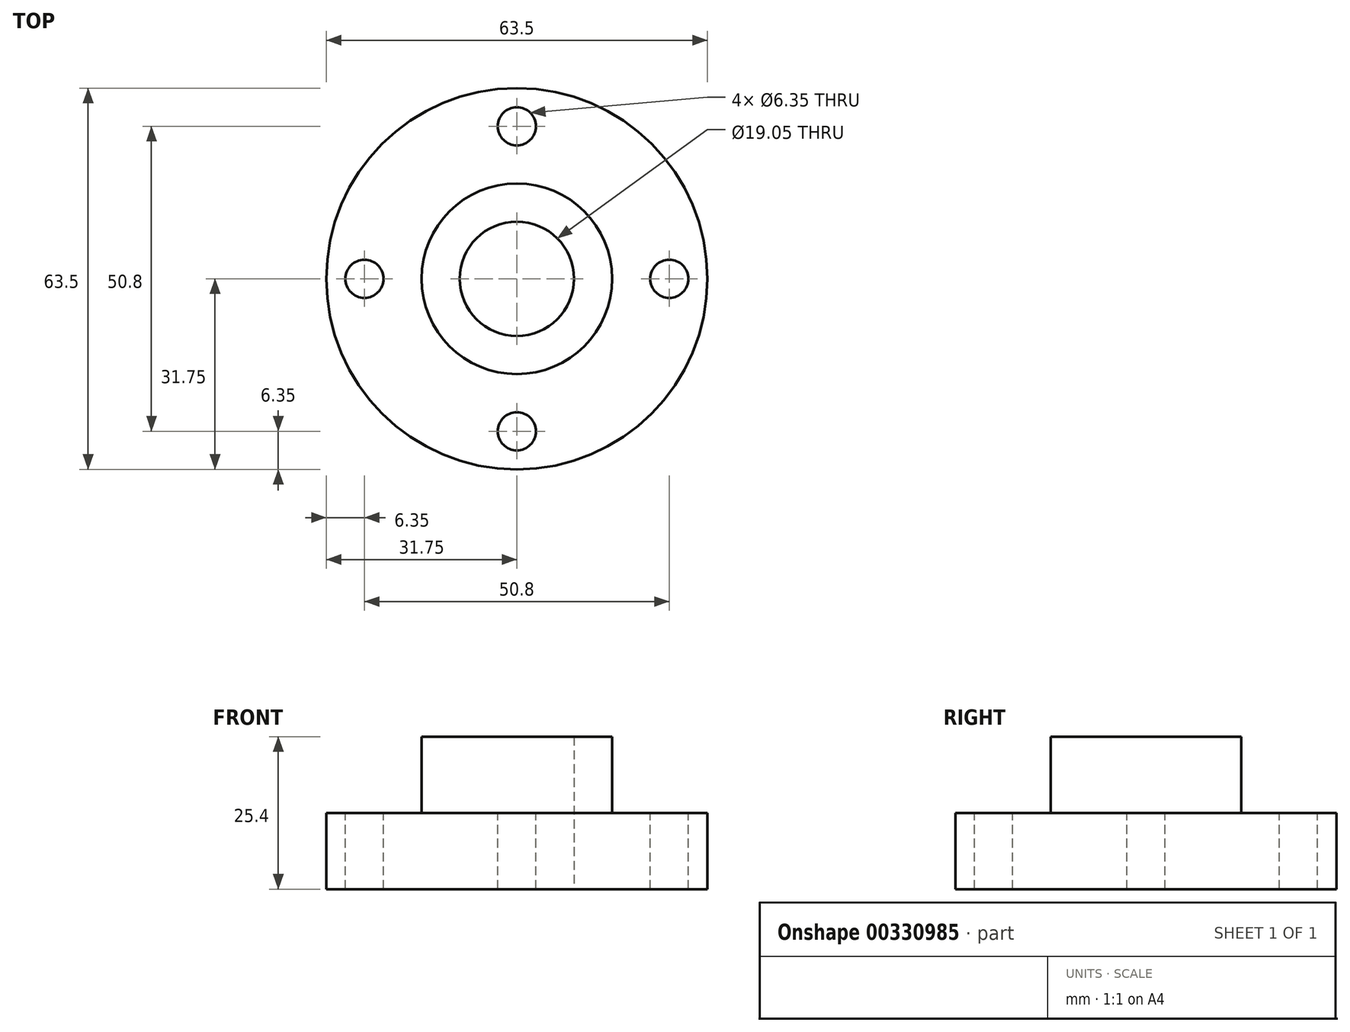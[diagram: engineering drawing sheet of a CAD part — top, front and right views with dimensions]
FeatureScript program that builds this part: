
annotation { "Feature Type Name" : "Feature", "Feature Type Description" : "" }
export const myFeature = defineFeature(function(context is Context, id is Id, definition is map)
    precondition{}
    {
        {
            var Q0;
            Q0=qCreatedBy(makeId("Top.planeOp"),FACE);
            var sketch = newSketch(context, id + "F0", { "sketchPlane" : qUnion([Q0])});
            skCircle(sketch, "E0", {"center": v(0, 0) * mm, "radius": 31.75 * mm});
            skCircle(sketch, "E1", {"center": v(0, 0) * mm, "radius": 25.4 * mm});
            skCircle(sketch, "E2", {"center": v(0, 25.4) * mm, "radius": 3.18 * mm});
            skCircle(sketch, "E3.1.0", {"center": v(-25.4, 0) * mm, "radius": 3.18 * mm});
            skCircle(sketch, "E3.2.0", {"center": v(0, -25.4) * mm, "radius": 3.18 * mm});
            skCircle(sketch, "E3.3.0", {"center": v(25.4, 0) * mm, "radius": 3.18 * mm});
            skSolve(sketch);
        }
        {
            var Q0;
            Q0=makeQuery(id+"F0.imprint","IMPRINT",FACE,{"disambiguationData":[TD([[makeQuery(id+"F0.imprint","IMPRINT",EDGE,{"derivedFrom":sQuery(id+"F0.wireOp",EDGE,"E0")}),1.0]])]});
            var Q1;
            {var subQ1=sQuery(id+"F0.wireOp",EDGE,"E1");var subQ8=sQuery(id+"F0.wireOp",EDGE,"E2");var subQ11=makeQuery(id+"F0.imprint","INTERSECT",VERTEX,{"disambiguationData":[OD(0.0)],"derivedFrom":[subQ1,subQ8]});Q1=makeQuery(id+"F0.imprint","IMPRINT",FACE,{"disambiguationData":[TD([[makeQuery(id+"F0.imprint","IMPRINT",EDGE,{"disambiguationData":[TD([[subQ11,1.0]])],"derivedFrom":subQ1}),1.0]])]});}
            extrude(context, id + "F1", {"entities" : qUnion([Q0, Q1]), "oppositeDirection" : true, "depth" : 12.7 * mm});
        }
        {
            var Q0;
            Q0=qCreatedBy(makeId("Top.planeOp"),FACE);
            var sketch = newSketch(context, id + "F2", { "sketchPlane" : qUnion([Q0])});
            skCircle(sketch, "E4", {"center": v(0, 0) * mm, "radius": 15.88 * mm});
            skCircle(sketch, "E5", {"center": v(0, 0) * mm, "radius": 9.53 * mm});
            skSolve(sketch);
        }
        {
            var Q0;
            Q0 = qSketchRegion(id + "F2", true);
            extrude(context, id + "F3", {"entities" : qUnion([Q0]), "operationType" : NewBodyOperationType.ADD, "depth" : 12.7 * mm});
        }
        {
            var Q0;
            Q0=makeQuery(id+"F3.boolean.opBoolean","SPLIT",FACE,{"disambiguationData":[TD([makeQuery(id+"F3.opExtrude","SWEPT_FACE",FACE,{"disambiguationData":[OSD([sQuery(id+"F2.wireOp",EDGE,"E5")])]})])],"derivedFrom":makeQuery(id+"F1.opExtrude","CAP_FACE",FACE,{"disambiguationData":[OSD([sQuery(id+"F0.wireOp",EDGE,"E0"),sQuery(id+"F0.wireOp",EDGE,"E2"),sQuery(id+"F0.wireOp",EDGE,"E3.1.0"),sQuery(id+"F0.wireOp",EDGE,"E3.2.0"),sQuery(id+"F0.wireOp",EDGE,"E3.3.0")])],"isStart":true})});
            extrude(context, id + "F4", {"entities" : qUnion([Q0]), "operationType" : NewBodyOperationType.REMOVE, "endBound" : BoundingType.THROUGH_ALL, "oppositeDirection" : true, "depth" : 25.4 * mm});
        }
    });
